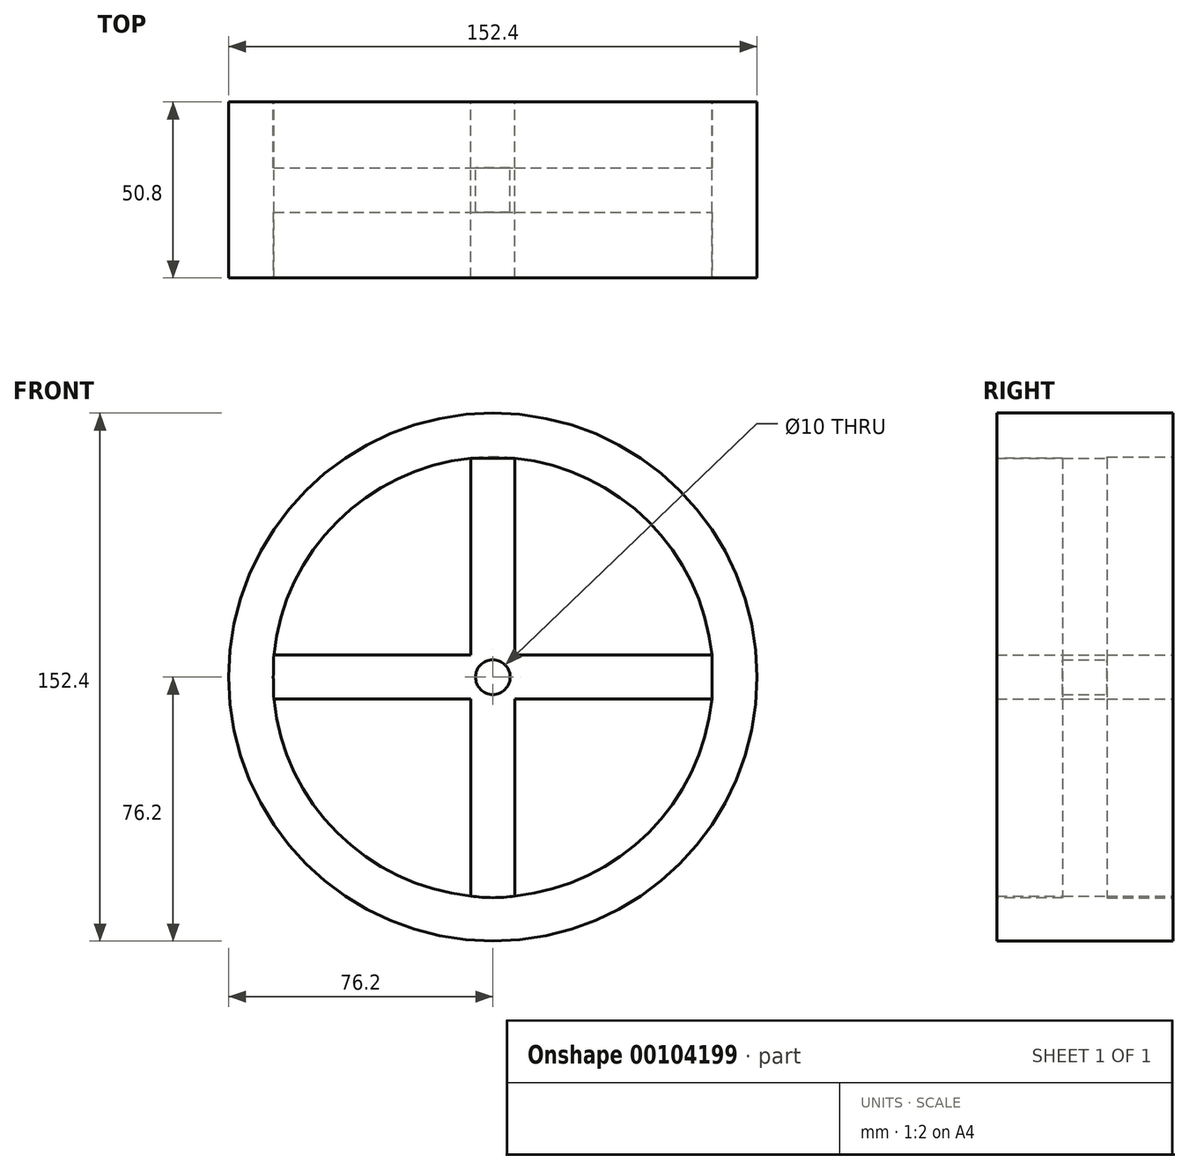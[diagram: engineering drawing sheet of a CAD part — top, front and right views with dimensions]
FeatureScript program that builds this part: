
annotation { "Feature Type Name" : "Feature", "Feature Type Description" : "" }
export const myFeature = defineFeature(function(context is Context, id is Id, definition is map)
    precondition{}
    {
        {
            var Q0;
            Q0=qCreatedBy(makeId("Front.planeOp"),FACE);
            var sketch = newSketch(context, id + "F0", { "sketchPlane" : qUnion([Q0])});
            skCircle(sketch, "E0", {"center": v(0, 0) * mm, "radius": 76.2 * mm});
            skArc(sketch, "E1", {"start": v(-6.35, 63.18) * mm, "mid": v(-63.5, 0) * mm, "end": v(-6.35, -63.18) * mm});
            skLineSegment(sketch, "E2.bottom", {"start": v(-6.35, 63.18) * mm, "end": v(6.35, 63.18) * mm});
            skLineSegment(sketch, "E2.left", {"start": v(-6.35, 63.18) * mm, "end": v(-6.35, 6.35) * mm});
            skLineSegment(sketch, "E2.right", {"start": v(6.35, 63.18) * mm, "end": v(6.35, 6.35) * mm});
            skLineSegment(sketch, "E3.bottom", {"start": v(-63.18, 6.35) * mm, "end": v(-6.35, 6.35) * mm});
            skLineSegment(sketch, "E3.top", {"start": v(-63.18, -6.35) * mm, "end": v(-6.35, -6.35) * mm});
            skLineSegment(sketch, "E3.right", {"start": v(63.18, 6.35) * mm, "end": v(63.18, -6.35) * mm});
            skLineSegment(sketch, "E4.trimOffspring", {"start": v(6.35, 6.35) * mm, "end": v(63.18, 6.35) * mm});
            skLineSegment(sketch, "E5.trimOffspring", {"start": v(6.35, -6.35) * mm, "end": v(63.18, -6.35) * mm});
            skLineSegment(sketch, "E6.trimOffspring", {"start": v(6.35, -6.35) * mm, "end": v(6.35, -63.18) * mm});
            skLineSegment(sketch, "E7.trimOffspring", {"start": v(-6.35, -6.35) * mm, "end": v(-6.35, -63.18) * mm});
            skCircle(sketch, "E8", {"center": v(0, 0) * mm, "radius": 5 * mm});
            skArc(sketch, "E9.trimOffspring", {"start": v(63.18, 6.35) * mm, "mid": v(44.9, 44.9) * mm, "end": v(6.35, 63.18) * mm});
            skArc(sketch, "E10.trimOffspring", {"start": v(6.35, -63.18) * mm, "mid": v(44.9, -44.9) * mm, "end": v(63.18, -6.35) * mm});
            skSolve(sketch);
        }
        {
            var Q0;
            Q0=makeQuery(id+"F0.imprint","IMPRINT",FACE,{"disambiguationData":[TD([[makeQuery(id+"F0.imprint","IMPRINT",EDGE,{"derivedFrom":sQuery(id+"F0.wireOp",EDGE,"E0")}),1.0]])]});
            extrude(context, id + "F1", {"entities" : qUnion([Q0]), "endBound" : BoundingType.SYMMETRIC, "depth" : 50.8 * mm});
        }
        {
            var Q0;
            Q0=makeQuery(id+"F1.opExtrude","CAP_FACE",FACE,{"disambiguationData":[OSD([sQuery(id+"F0.wireOp",EDGE,"E0"),sQuery(id+"F0.wireOp",EDGE,"E1"),sQuery(id+"F0.wireOp",EDGE,"E2.left"),sQuery(id+"F0.wireOp",EDGE,"E2.right"),sQuery(id+"F0.wireOp",EDGE,"E3.bottom"),sQuery(id+"F0.wireOp",EDGE,"E3.top"),sQuery(id+"F0.wireOp",EDGE,"E4.trimOffspring"),sQuery(id+"F0.wireOp",EDGE,"E5.trimOffspring"),sQuery(id+"F0.wireOp",EDGE,"E6.trimOffspring"),sQuery(id+"F0.wireOp",EDGE,"E7.trimOffspring"),sQuery(id+"F0.wireOp",EDGE,"E8"),sQuery(id+"F0.wireOp",EDGE,"E9.trimOffspring"),sQuery(id+"F0.wireOp",EDGE,"E10.trimOffspring")])],"isStart":false});
            var sketch = newSketch(context, id + "F2", { "sketchPlane" : qUnion([Q0])});
            skArc(sketch, "E11", {"start": v(-63.18, 6.35) * mm, "mid": v(-63.32, 0) * mm, "end": v(-63.18, -6.35) * mm});
            skArc(sketch, "E12", {"start": v(63.18, -6.35) * mm, "mid": v(63.27, 0) * mm, "end": v(63.18, 6.35) * mm});
            skArc(sketch, "E13", {"start": v(6.35, 63.18) * mm, "mid": v(0, 63.21) * mm, "end": v(-6.35, 63.18) * mm});
            skArc(sketch, "E14", {"start": v(-6.35, -63.18) * mm, "mid": v(0, -63.65) * mm, "end": v(6.35, -63.18) * mm});
            skSolve(sketch);
        }
        {
            var Q0;
            Q0=makeQuery(id+"F2.imprint","IMPRINT",FACE,{"disambiguationData":[TD([[makeQuery(id+"F2.imprint","IMPRINT",EDGE,{"derivedFrom":sQuery(id+"F2.wireOp",EDGE,"E11")}),1.0]])]});
            extrude(context, id + "F3", {"entities" : qUnion([Q0]), "operationType" : NewBodyOperationType.REMOVE, "oppositeDirection" : true, "depth" : 19 * mm});
        }
        {
            var Q0;
            Q0=makeQuery(id+"F1.opExtrude","CAP_FACE",FACE,{"disambiguationData":[OSD([sQuery(id+"F0.wireOp",EDGE,"E0"),sQuery(id+"F0.wireOp",EDGE,"E1"),sQuery(id+"F0.wireOp",EDGE,"E2.left"),sQuery(id+"F0.wireOp",EDGE,"E2.right"),sQuery(id+"F0.wireOp",EDGE,"E3.bottom"),sQuery(id+"F0.wireOp",EDGE,"E3.top"),sQuery(id+"F0.wireOp",EDGE,"E4.trimOffspring"),sQuery(id+"F0.wireOp",EDGE,"E5.trimOffspring"),sQuery(id+"F0.wireOp",EDGE,"E6.trimOffspring"),sQuery(id+"F0.wireOp",EDGE,"E7.trimOffspring"),sQuery(id+"F0.wireOp",EDGE,"E8"),sQuery(id+"F0.wireOp",EDGE,"E9.trimOffspring"),sQuery(id+"F0.wireOp",EDGE,"E10.trimOffspring")])],"isStart":true});
            var sketch = newSketch(context, id + "F4", { "sketchPlane" : qUnion([Q0])});
            skArc(sketch, "E15", {"start": v(6.35, 63.18) * mm, "mid": v(0, 63.52) * mm, "end": v(-6.35, 63.18) * mm});
            skArc(sketch, "E16", {"start": v(63.18, -6.35) * mm, "mid": v(63.43, 0) * mm, "end": v(63.18, 6.35) * mm});
            skArc(sketch, "E17", {"start": v(-63.18, 6.35) * mm, "mid": v(-63.4, 0) * mm, "end": v(-63.18, -6.35) * mm});
            skArc(sketch, "E18", {"start": v(-6.35, -63.18) * mm, "mid": v(0, -63.74) * mm, "end": v(6.35, -63.18) * mm});
            skSolve(sketch);
        }
        {
            var Q0;
            Q0=makeQuery(id+"F4.imprint","IMPRINT",FACE,{"disambiguationData":[TD([[makeQuery(id+"F4.imprint","IMPRINT",EDGE,{"derivedFrom":sQuery(id+"F4.wireOp",EDGE,"E15")}),1.0]])]});
            extrude(context, id + "F5", {"entities" : qUnion([Q0]), "operationType" : NewBodyOperationType.REMOVE, "oppositeDirection" : true, "depth" : 19 * mm});
        }
    });
